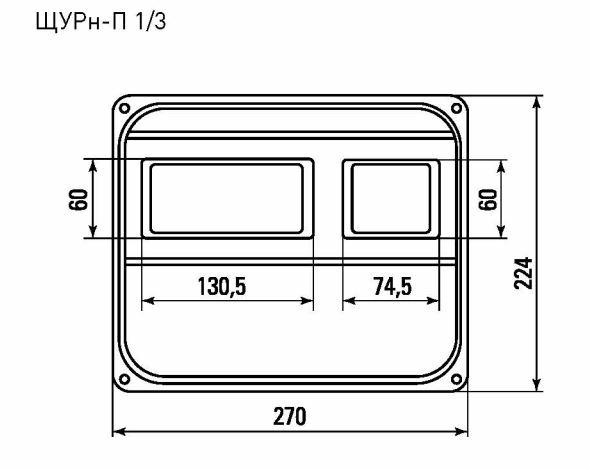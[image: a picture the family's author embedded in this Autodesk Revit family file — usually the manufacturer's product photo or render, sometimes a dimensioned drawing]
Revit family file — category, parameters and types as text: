
# Revit family: EKF_EE_ЩУРн-П_IP55_PROxima
name_source: partatom
category: Электрооборудование
units: mm (PartAtom-declared; Revit-internal decimal feet)

## family parameters
Всегда вертикально = Да
На основе рабочей плоскости = Нет
Общий = Нет
При загрузке вырезать с полостями = Нет
Размер круглого соединителя = Использовать диаметр
Тип детали = Силовой щит
Точка расчета площади = Да

## types (3) — shared parameters
ADSK_Единица измерения = компл.
ADSK_Завод-изготовитель = EKF
ADSK_Классификация нагрузок = Прочее
ADSK_Количество = 1
ADSK_Количество фаз = 1
ADSK_Коэффициент мощности = 1
ADSK_Материал = Белый_ABS-пластик
ADSK_Напряжение = 400 В
ADSK_Номинальная мощность = 0 Вт
ADSK_Полная мощность = 0 В·А
ADSK_Ток = 125 А
Изготовитель = EKF
Количество DIN-реек = 1
Серия номенклатуры = PROxima
Степень защиты IP = IP55
ТВ = EKF
Тип установки = Навесной
zero-valued in all types: ADSK_Масса

## per-type parameters (varying)
| type | ADSK_Код изделия | ADSK_Марка | ADSK_Наименование | ADSK_Обозначение | ADSK_Размер_Высота | ADSK_Размер_Глубина | ADSK_Размер_Ширина | Количество модулей на DIN-рейке | Максимальное количество модулей | Описание | Тип |
| ЩУРн-П 3/8 (379х216х113) IP55 EKF PROxima | pb-3/8-55 | ЩУРн-П 3/8 IP55 | Щит учетно-распред. навесной пластик ЩУРн-П 3/8 (379х216х113) IP55 EKF PROxima | ЩУРн-П 3/8 IP55 | 379 мм | 113 мм | 216 мм | 8 | 2 | Щит учетно-распред. навесной пластик ЩУРн-П 3/8 (379х216х113) IP55 EKF PROxima | 5 мм |
| ЩУРн-П 1/5 (229х340х117) IP55 EKF PROxima | pb-1/5-55 | ЩУРн-П 1/5 IP55 | Щит учетно-распред. навесной пластик ЩУРн-П 1/5 (229х340х117) IP55 EKF PROxima | ЩУРн-П 1/5 IP55 | 229 мм | 117 мм | 340 мм | 5 | 2 | Щит учетно-распред. навесной пластик ЩУРн-П 1/5 (229х340х117) IP55 EKF PROxima | 6 мм |
| ЩУРн-П 3/11 (494х300х136) IP55 EKF PROxima | pb-3/11-55 | ЩУРн-П 3/11 IP55 | Щит учетно-распред. навесной пластик ЩУРн-П 3/11 (494х300х136) IP55 EKF PROxima | ЩУРн-П 3/11 IP55 | 494 мм | 136 мм | 300 мм | 11 | 3 | Щит учетно-распред. навесной пластик ЩУРн-П 3/11 (494х300х136) IP55 EKF PROxima | 7 мм |
